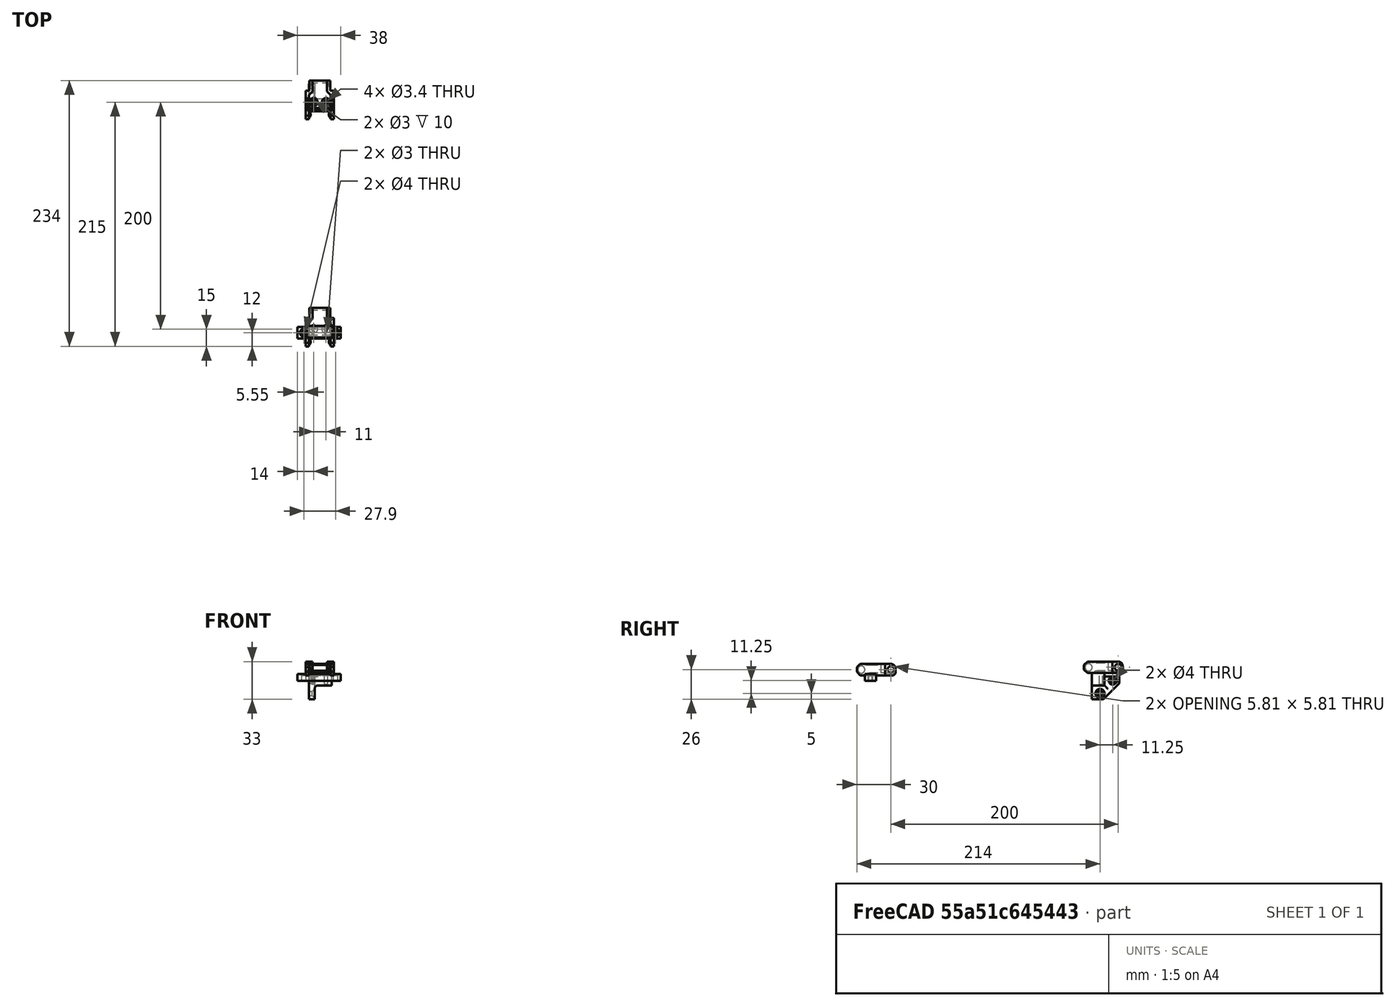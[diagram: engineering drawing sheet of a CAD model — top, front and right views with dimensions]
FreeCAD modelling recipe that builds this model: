
FCSTD DOCUMENT  (FreeCAD 0.18R16146 (Git))
Label: Cable Chain Mount 0.1
License: All rights reserved
LicenseURL: http://en.wikipedia.org/wiki/All_rights_reserved
objects: Part::Box×24, Part::Cut×20, Part::Chamfer×18, Part::Cylinder×12, Part::MultiFuse×11, Part::Sphere×8, Part::Mirroring×6, Part::Fillet×4, Part::Fuse×2
note: 105 computed .brp shape members not serialized (recipe doc carries the construction recipe); baked Part::Feature solids carry a one-line shape summary decoded from their .brp

FEATURE [Part::Box] Box  label="Cube"
  AttacherType = Attacher::AttachEngine3D
  Height = 10
  Length = 25
  Width = 25
FEATURE [Part::Box] Box001  label="Cube001"
  AttacherType = Attacher::AttachEngine3D
  Height = 10
  Length = 19
  Placement = pos=(3,-1,2) rot=(0,0,1;0rad)
  Width = 28
FEATURE [Part::Cut] Cut
  Base = -> Box
  Tool = -> Box001
FEATURE [Part::Box] Box002  label="Cube002"
  AttacherType = Attacher::AttachEngine3D
  Height = 10
  Length = 19
  Placement = pos=(3,0,-4) rot=(0,0,1;0rad)
  Width = 8
FEATURE [Part::Cut] Cut001
  Base = -> Cut
  Tool = -> Box002
FEATURE [Part::Sphere] Sphere
  Angle1 = -90
  Angle2 = 90
  Angle3 = 360
  AttacherType = Attacher::AttachEngine3D
  Placement = pos=(0,4,5) rot=(0,0,1;0rad)
  Radius = 4
FEATURE [Part::Box] Box003  label="Cube003"
  AttacherType = Attacher::AttachEngine3D
  Height = 10
  Length = 10
  Placement = pos=(-8,0,0) rot=(0,0,1;0rad)
  Width = 10
FEATURE [Part::Cut] Cut002
  Base = -> Sphere
  Placement = pos=(0.5,0,0) rot=(0,0,1;0rad)
  Tool = -> Box003
FEATURE [Part::Box] Box004  label="Cube004"
  AttacherType = Attacher::AttachEngine3D
  Height = 10
  Length = 10
  Placement = pos=(-8,0,0) rot=(0,0,1;0rad)
  Width = 10
FEATURE [Part::Sphere] Sphere001
  Angle1 = -90
  Angle2 = 90
  Angle3 = 360
  AttacherType = Attacher::AttachEngine3D
  Placement = pos=(0,4,5) rot=(0,0,1;0rad)
  Radius = 4
FEATURE [Part::Cut] Cut003
  Base = -> Sphere001
  Tool = -> Box004
FEATURE [Part::Mirroring] Part__Mirroring  label="Cut003 (Mirror #1)"
  Base = (12.5,0,0)
  Normal = (1,0,0)
  Placement = pos=(-0.5,0,0) rot=(0,0,1;0rad)
  Source = -> Cut003
FEATURE [Part::Box] Box005  label="Cube005"
  AttacherType = Attacher::AttachEngine3D
  Height = 10
  Length = 18.5
  Placement = pos=(3.25,24,0) rot=(0,0,1;0rad)
  Width = 10
FEATURE [Part::Sphere] Sphere002
  Angle1 = -90
  Angle2 = 90
  Angle3 = 360
  AttacherType = Attacher::AttachEngine3D
  Placement = pos=(0.5,4,5) rot=(0,0,1;0rad)
  Radius = 4
FEATURE [Part::Sphere] Sphere003
  Angle1 = -90
  Angle2 = 90
  Angle3 = 360
  AttacherType = Attacher::AttachEngine3D
  Placement = pos=(0.5,4,5) rot=(0,0,1;0rad)
  Radius = 4
FEATURE [Part::Mirroring] Part__Mirroring001  label="Sphere003 (Mirror #2)"
  Base = (12.5,0,0)
  Normal = (1,0,0)
  Source = -> Sphere003
FEATURE [Part::MultiFuse] Fusion001
  Placement = pos=(0,26,0) rot=(0,0,1;0rad)
  Shapes = -> [Sphere002,Part__Mirroring001]
FEATURE [Part::Box] Box006  label="Cube006"
  AttacherType = Attacher::AttachEngine3D
  Height = 10
  Length = 12.5
  Placement = pos=(6.25,23,2) rot=(0,0,1;0rad)
  Width = 12
FEATURE [Part::Cut] Cut004
  Base = -> Box005
  Tool = -> Box006
FEATURE [Part::Cut] Cut005
  Base = -> Cut004
  Tool = -> Fusion001
FEATURE [Part::Box] Box007  label="Cube007"
  AttacherType = Attacher::AttachEngine3D
  Height = 10
  Length = 6.25
  Placement = pos=(0,21,0) rot=(0,0,1;0rad)
  Width = 4
FEATURE [Part::Chamfer] Chamfer001
  Base = -> Box007
  Edges = 1 edges r=3.5: [Edge5]
FEATURE [Part::Chamfer] Chamfer002
  Base = -> Cut005
  Edges = 2 edges r=1: [Edge9,Edge11]
FEATURE [Part::Box] Box008  label="Cube008"
  AttacherType = Attacher::AttachEngine3D
  Height = 10
  Length = 6.25
  Placement = pos=(0,21,0) rot=(0,0,1;0rad)
  Width = 4
FEATURE [Part::Chamfer] Chamfer003
  Base = -> Box008
  Edges = 1 edges r=3.5: [Edge5]
FEATURE [Part::Mirroring] Part__Mirroring002  label="Chamfer003 (Mirror #3)"
  Base = (12.5,0,0)
  Normal = (1,0,0)
  Source = -> Chamfer003
FEATURE [Part::Box] Box010  label="Cube010"
  AttacherType = Attacher::AttachEngine3D
  Height = 2
  Length = 23
  Placement = pos=(1,7.8,8.8) rot=(0,0,1;0rad)
  Width = 10.4
FEATURE [Part::Box] Box011  label="lid"
  AttacherType = Attacher::AttachEngine3D
  Height = 1
  Length = 22.5
  Placement = pos=(1.25,8,9) rot=(0,0,1;0rad)
  Width = 10
FEATURE [Part::Cylinder] Cylinder
  Angle = 360
  AttacherType = Attacher::AttachEngine3D
  Height = 10
  Placement = pos=(7,12,-8) rot=(0,0,1;0rad)
  Radius = 1.7
FEATURE [Part::Cylinder] Cylinder001
  Angle = 360
  AttacherType = Attacher::AttachEngine3D
  Height = 10
  Placement = pos=(18,12,-8) rot=(0,0,1;0rad)
  Radius = 1.7
FEATURE [Part::MultiFuse] Fusion003
  Placement = pos=(0,3,2) rot=(0,0,1;0rad)
  Shapes = -> [Cylinder,Cylinder001]
FEATURE [Part::MultiFuse] Fusion
  Shapes = -> [Cut001,Part__Mirroring,Cut002]
FEATURE [Part::Chamfer] Chamfer
  Base = -> Fusion
  Edges = 4 edges r=3: [Edge8,Edge9,Edge19,Edge37]
FEATURE [Part::MultiFuse] Fusion004
  Shapes = -> [Chamfer001,Chamfer002,Part__Mirroring002,Chamfer]
FEATURE [Part::Cut] Cut006
  Base = -> Fusion004
  Tool = -> Box010
FEATURE [Part::Cut] Cut007
  Base = -> Cut006
  Tool = -> Fusion003
FEATURE [Part::Chamfer] Chamfer004  label="link-a"
  Base = -> Cut007
  Edges = 2 edges r=1.9: [Edge49,Edge50]
FEATURE [Part::Chamfer] Chamfer005
  Base = -> Chamfer004
  Edges = 1 edges r=1.9: [Edge3]
FEATURE [Part::Chamfer] Chamfer006  label="link-b"
  Base = -> Chamfer005
  Edges = 1 edges r=1.9: [Edge161]
FEATURE [Part::Fillet] Fillet  label="Cable Chain 0.1"
  Base = -> Chamfer006
  Edges = 2 edges r=4: [Edge3,Edge6]
FEATURE [Part::Cylinder] Cylinder002
  Angle = 360
  AttacherType = Attacher::AttachEngine3D
  Height = 10
  Placement = pos=(18,12,-8) rot=(0,0,1;0rad)
  Radius = 1.5
FEATURE [Part::Cylinder] Cylinder003
  Angle = 360
  AttacherType = Attacher::AttachEngine3D
  Height = 10
  Placement = pos=(7,12,-8) rot=(0,0,1;0rad)
  Radius = 1.5
FEATURE [Part::Cylinder] Cylinder004
  Angle = 360
  AttacherType = Attacher::AttachEngine3D
  Height = 10
  Placement = pos=(26.45,12,-8) rot=(0,0,1;0rad)
  Radius = 2
FEATURE [Part::Cylinder] Cylinder005
  Angle = 360
  AttacherType = Attacher::AttachEngine3D
  Height = 10
  Placement = pos=(-1.45,12,-8) rot=(0,0,1;0rad)
  Radius = 2
FEATURE [Part::Box] Box012  label="Cube011"
  AttacherType = Attacher::AttachEngine3D
  Height = 6
  Length = 38
  Placement = pos=(-7,7,-5) rot=(0,0,1;0rad)
  Width = 10
FEATURE [Part::MultiFuse] Fusion005
  Shapes = -> [Cylinder004,Cylinder005]
FEATURE [Part::Fuse] Fusion006
  Base = -> Cylinder002
  Tool = -> Cylinder003
FEATURE [Part::Cut] Cut008
  Base = -> Box012
  Tool = -> Fusion005
FEATURE [Part::Cut] Cut009
  Base = -> Cut008
  Tool = -> Fusion006
FEATURE [Part::Chamfer] Chamfer007  label="Cable Chain Mount Electronics End 0.1"
  Base = -> Cut009
  Edges = 2 edges r=1.5: [Edge10,Edge13]
FEATURE [Part::Box] Box013  label="Cube012"
  AttacherType = Attacher::AttachEngine3D
  Height = 10
  Length = 10
  Placement = pos=(-8,0,0) rot=(0,0,1;0rad)
  Width = 10
FEATURE [Part::Box] Box014  label="Cube013"
  AttacherType = Attacher::AttachEngine3D
  Height = 10
  Length = 19
  Placement = pos=(3,-1,2) rot=(0,0,1;0rad)
  Width = 28
FEATURE [Part::Box] Box015  label="Cube014"
  AttacherType = Attacher::AttachEngine3D
  Height = 10
  Length = 25
  Width = 25
FEATURE [Part::Cut] Cut011
  Base = -> Box015
  Tool = -> Box014
FEATURE [Part::Box] Box016  label="Cube015"
  AttacherType = Attacher::AttachEngine3D
  Height = 10
  Length = 19
  Placement = pos=(3,0,-4) rot=(0,0,1;0rad)
  Width = 8
FEATURE [Part::Cylinder] Cylinder006
  Angle = 360
  AttacherType = Attacher::AttachEngine3D
  Height = 10
  Placement = pos=(7,12,-8) rot=(0,0,1;0rad)
  Radius = 1.7
FEATURE [Part::Box] Box017  label="Cube016"
  AttacherType = Attacher::AttachEngine3D
  Height = 10
  Length = 6.25
  Placement = pos=(0,21,0) rot=(0,0,1;0rad)
  Width = 4
FEATURE [Part::Chamfer] Chamfer008
  Base = -> Box017
  Edges = 1 edges r=3.5: [Edge5]
FEATURE [Part::Mirroring] Part__Mirroring003  label="Chamfer003 (Mirror #3)001"
  Base = (12.5,0,0)
  Normal = (1,0,0)
  Source = -> Chamfer008
FEATURE [Part::Sphere] Sphere004
  Angle1 = -90
  Angle2 = 90
  Angle3 = 360
  AttacherType = Attacher::AttachEngine3D
  Placement = pos=(0,4,5) rot=(0,0,1;0rad)
  Radius = 4
FEATURE [Part::Sphere] Sphere005
  Angle1 = -90
  Angle2 = 90
  Angle3 = 360
  AttacherType = Attacher::AttachEngine3D
  Placement = pos=(0.5,4,5) rot=(0,0,1;0rad)
  Radius = 4
FEATURE [Part::Cut] Cut013
  Base = -> Cut011
  Tool = -> Box016
FEATURE [Part::Box] Box018  label="Cube017"
  AttacherType = Attacher::AttachEngine3D
  Height = 2
  Length = 23
  Placement = pos=(1,7.8,8.8) rot=(0,0,1;0rad)
  Width = 10.4
FEATURE [Part::Sphere] Sphere006
  Angle1 = -90
  Angle2 = 90
  Angle3 = 360
  AttacherType = Attacher::AttachEngine3D
  Placement = pos=(0,4,5) rot=(0,0,1;0rad)
  Radius = 4
FEATURE [Part::Cylinder] Cylinder007
  Angle = 360
  AttacherType = Attacher::AttachEngine3D
  Height = 10
  Placement = pos=(18,12,-8) rot=(0,0,1;0rad)
  Radius = 1.7
FEATURE [Part::MultiFuse] Fusion008
  Placement = pos=(0,3,2) rot=(0,0,1;0rad)
  Shapes = -> [Cylinder006,Cylinder007]
FEATURE [Part::Box] Box019  label="Cube018"
  AttacherType = Attacher::AttachEngine3D
  Height = 10
  Length = 18.5
  Placement = pos=(3.25,24,0) rot=(0,0,1;0rad)
  Width = 10
FEATURE [Part::Sphere] Sphere007
  Angle1 = -90
  Angle2 = 90
  Angle3 = 360
  AttacherType = Attacher::AttachEngine3D
  Placement = pos=(0.5,4,5) rot=(0,0,1;0rad)
  Radius = 4
FEATURE [Part::Cut] Cut015
  Base = -> Sphere006
  Placement = pos=(0.5,0,0) rot=(0,0,1;0rad)
  Tool = -> Box013
FEATURE [Part::Box] Box020  label="Cube019"
  AttacherType = Attacher::AttachEngine3D
  Height = 10
  Length = 12.5
  Placement = pos=(6.25,23,2) rot=(0,0,1;0rad)
  Width = 12
FEATURE [Part::Cut] Cut014
  Base = -> Box019
  Tool = -> Box020
FEATURE [Part::Box] Box021  label="Cube020"
  AttacherType = Attacher::AttachEngine3D
  Height = 10
  Length = 10
  Placement = pos=(-8,0,0) rot=(0,0,1;0rad)
  Width = 10
FEATURE [Part::Cut] Cut010
  Base = -> Sphere004
  Tool = -> Box021
FEATURE [Part::Mirroring] Part__Mirroring004  label="Sphere003 (Mirror #2)001"
  Base = (12.5,0,0)
  Normal = (1,0,0)
  Source = -> Sphere005
FEATURE [Part::MultiFuse] Fusion009
  Placement = pos=(0,26,0) rot=(0,0,1;0rad)
  Shapes = -> [Sphere007,Part__Mirroring004]
FEATURE [Part::Cut] Cut017
  Base = -> Cut014
  Tool = -> Fusion009
FEATURE [Part::Chamfer] Chamfer013
  Base = -> Cut017
  Edges = 2 edges r=1: [Edge9,Edge11]
FEATURE [Part::Mirroring] Part__Mirroring005  label="Cut003 (Mirror #1)001"
  Base = (12.5,0,0)
  Normal = (1,0,0)
  Placement = pos=(-0.5,0,0) rot=(0,0,1;0rad)
  Source = -> Cut010
FEATURE [Part::MultiFuse] Fusion010
  Shapes = -> [Cut013,Part__Mirroring005,Cut015]
FEATURE [Part::Chamfer] Chamfer012
  Base = -> Fusion010
  Edges = 4 edges r=3: [Edge8,Edge9,Edge19,Edge37]
FEATURE [Part::Box] Box022  label="Cube021"
  AttacherType = Attacher::AttachEngine3D
  Height = 10
  Length = 6.25
  Placement = pos=(0,21,0) rot=(0,0,1;0rad)
  Width = 4
FEATURE [Part::Chamfer] Chamfer014
  Base = -> Box022
  Edges = 1 edges r=3.5: [Edge5]
FEATURE [Part::MultiFuse] Fusion007
  Shapes = -> [Chamfer014,Chamfer013,Part__Mirroring003,Chamfer012]
FEATURE [Part::Cut] Cut012
  Base = -> Fusion007
  Tool = -> Box018
FEATURE [Part::Cut] Cut016
  Base = -> Cut012
  Tool = -> Fusion008
FEATURE [Part::Chamfer] Chamfer009  label="link-a001"
  Base = -> Cut016
  Edges = 2 edges r=1.9: [Edge49,Edge50]
FEATURE [Part::Chamfer] Chamfer010
  Base = -> Chamfer009
  Edges = 1 edges r=1.9: [Edge3]
FEATURE [Part::Chamfer] Chamfer011  label="link-b001"
  Base = -> Chamfer010
  Edges = 1 edges r=1.9: [Edge161]
FEATURE [Part::Fillet] Fillet001  label="Copy Cable Chain 0.1"
  Base = -> Chamfer011
  Edges = 2 edges r=4: [Edge3,Edge6]
  Placement = pos=(0,200,2) rot=(0,0,1;0rad)
FEATURE [Part::Cylinder] Cylinder008
  Angle = 360
  AttacherType = Attacher::AttachEngine3D
  Height = 10
  Placement = pos=(0,214,-16) rot=(0,1,0;1.5708rad)
  Radius = 2
FEATURE [Part::Box] Box023  label="Cube022"
  AttacherType = Attacher::AttachEngine3D
  Height = 20
  Length = 5
  Placement = pos=(3,207,-21) rot=(0,0,1;0rad)
  Width = 24
FEATURE [Part::Cylinder] Cylinder009
  Angle = 360
  AttacherType = Attacher::AttachEngine3D
  Height = 10
  Placement = pos=(0,225.25,-4.75) rot=(0.357407,0.862856,0.357407;1.71777rad)
  Radius = 2
FEATURE [Part::Box] Box024  label="Cube023"
  AttacherType = Attacher::AttachEngine3D
  Height = 11
  Length = 20
  Placement = pos=(3,207,-9) rot=(0,0,1;0rad)
  Width = 11
FEATURE [Part::Cylinder] Cylinder010
  Angle = 360
  AttacherType = Attacher::AttachEngine3D
  Height = 10
  Placement = pos=(18,215,-8) rot=(0,0,1;0rad)
  Radius = 1.5
FEATURE [Part::Cylinder] Cylinder011
  Angle = 360
  AttacherType = Attacher::AttachEngine3D
  Height = 14
  Placement = pos=(7,215,-8) rot=(0,0,1;0rad)
  Radius = 1.5
FEATURE [Part::Fuse] Fusion011
  Base = -> Box023
  Tool = -> Box024
FEATURE [Part::MultiFuse] Fusion012
  Shapes = -> [Cylinder009,Cylinder008]
FEATURE [Part::MultiFuse] Fusion013
  Shapes = -> [Cylinder011,Cylinder010]
FEATURE [Part::Fillet] Fillet002
  Base = -> Fusion011
  Edges = 1 edges r=3: [Edge18]
FEATURE [Part::Fillet] Fillet003
  Base = -> Fillet002
  Edges = 1 edges r=3: [Edge10]
FEATURE [Part::Cut] Cut018
  Base = -> Fillet003
  Tool = -> Fusion013
FEATURE [Part::Cut] Cut019
  Base = -> Cut018
  Tool = -> Fusion012
FEATURE [Part::Chamfer] Chamfer015
  Base = -> Cut019
  Edges = 1 edges r=1.5: [Edge9]
FEATURE [Part::Chamfer] Chamfer016  label="chamf16"
  Base = -> Chamfer015
  Edges = 1 edges r=2: [Edge10]
FEATURE [Part::Chamfer] Chamfer017  label="cable chain mount bed end 0.2"
  Base = -> Chamfer016
  Edges = 1 edges r=14: [Edge22]
